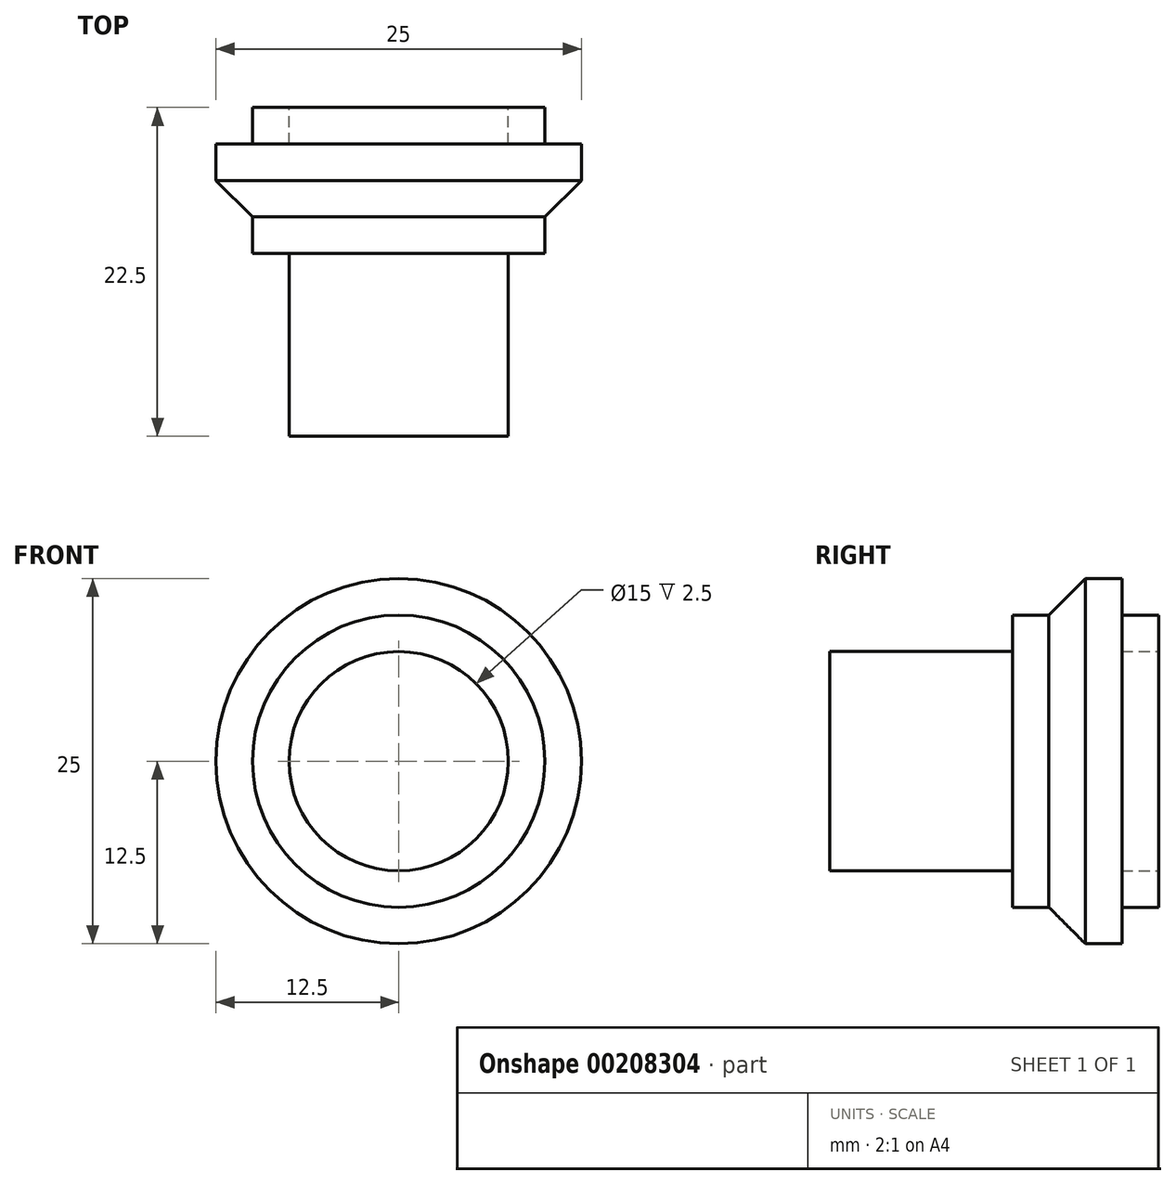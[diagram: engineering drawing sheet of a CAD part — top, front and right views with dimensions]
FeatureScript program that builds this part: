
annotation { "Feature Type Name" : "Feature", "Feature Type Description" : "" }
export const myFeature = defineFeature(function(context is Context, id is Id, definition is map)
    precondition{}
    {
        {
            var Q0;
            Q0=qCreatedBy(makeId("Front.planeOp"),FACE);
            var sketch = newSketch(context, id + "F0", { "sketchPlane" : qUnion([Q0])});
            skCircle(sketch, "E0", {"center": v(0, 0) * mm, "radius": 10 * mm});
            skCircle(sketch, "E1", {"center": v(0, 0) * mm, "radius": 7.5 * mm});
            skSolve(sketch);
        }
        {
            var Q0;
            Q0 = qSketchRegion(id + "F0", true);
            extrude(context, id + "F1", {"entities" : qUnion([Q0]), "depth" : 2.5 * mm});
        }
        {
            var Q0;
            Q0=qCreatedBy(makeId("Front.planeOp"),FACE);
            var sketch = newSketch(context, id + "F2", { "sketchPlane" : qUnion([Q0])});
            skCircle(sketch, "E2", {"center": v(0, 0) * mm, "radius": 10 * mm});
            skCircle(sketch, "E3", {"center": v(0, 0) * mm, "radius": 12.5 * mm});
            skSolve(sketch);
        }
        {
            var Q0;
            Q0=makeQuery(id+"F1.opExtrude","CAP_FACE",FACE,{"disambiguationData":[OSD([sQuery(id+"F0.wireOp",EDGE,"E0"),sQuery(id+"F0.wireOp",EDGE,"E1")])],"isStart":false});
            var Q1;
            Q1=makeQuery(id+"F2.imprint","IMPRINT",FACE,{"disambiguationData":[TD([[makeQuery(id+"F2.imprint","IMPRINT",EDGE,{"derivedFrom":sQuery(id+"F2.wireOp",EDGE,"E2")}),-1.0]])]});
            extrude(context, id + "F3", {"entities" : qUnion([Q0, Q1]), "operationType" : NewBodyOperationType.ADD, "depth" : 5 * mm});
        }
        {
            var Q0;
            Q0=qCreatedBy(makeId("Front.planeOp"),FACE);
            var sketch = newSketch(context, id + "F4", { "sketchPlane" : qUnion([Q0])});
            skCircle(sketch, "E4", {"center": v(0, 0) * mm, "radius": 7.5 * mm});
            skCircle(sketch, "E5", {"center": v(0, 0) * mm, "radius": 10 * mm});
            skSolve(sketch);
        }
        {
            var Q0;
            Q0 = qSketchRegion(id + "F4", true);
            extrude(context, id + "F5", {"entities" : qUnion([Q0]), "operationType" : NewBodyOperationType.ADD, "oppositeDirection" : true, "depth" : 2.5 * mm});
        }
        {
            var Q0;
            Q0=qCreatedBy(makeId("Front.planeOp"),FACE);
            var sketch = newSketch(context, id + "F6", { "sketchPlane" : qUnion([Q0])});
            skCircle(sketch, "E6", {"center": v(0, 0) * mm, "radius": 7.5 * mm});
            skCircle(sketch, "E7", {"center": v(0, 0) * mm, "radius": 12.5 * mm});
            skSolve(sketch);
        }
        {
            var Q0;
            Q0=makeQuery(id+"F3.opExtrude","CAP_EDGE",EDGE,{"disambiguationData":[OSD([sQuery(id+"F2.wireOp",EDGE,"E3")])],"isStart":false});
            chamfer(context, id + "F7", {"entities" : qUnion([Q0]), "width" : 2.5 * mm, "tangentPropagation" : true});
        }
        {
            var Q0;
            Q0=qCreatedBy(makeId("Front.planeOp"),FACE);
            var sketch = newSketch(context, id + "F8", { "sketchPlane" : qUnion([Q0])});
            skCircle(sketch, "E8", {"center": v(0, 0) * mm, "radius": 5 * mm});
            skSolve(sketch);
        }
        {
            var Q0;
            Q0 = qSketchRegion(id + "F8", true);
            var Q1;
            Q1=makeQuery(id+"F6.imprint","IMPRINT",FACE,{"disambiguationData":[TD([[makeQuery(id+"F6.imprint","IMPRINT",EDGE,{"derivedFrom":sQuery(id+"F6.wireOp",EDGE,"E6")}),1.0]])]});
            extrude(context, id + "F9", {"entities" : qUnion([Q0, Q1]), "operationType" : NewBodyOperationType.ADD, "depth" : 20 * mm});
        }
    });
